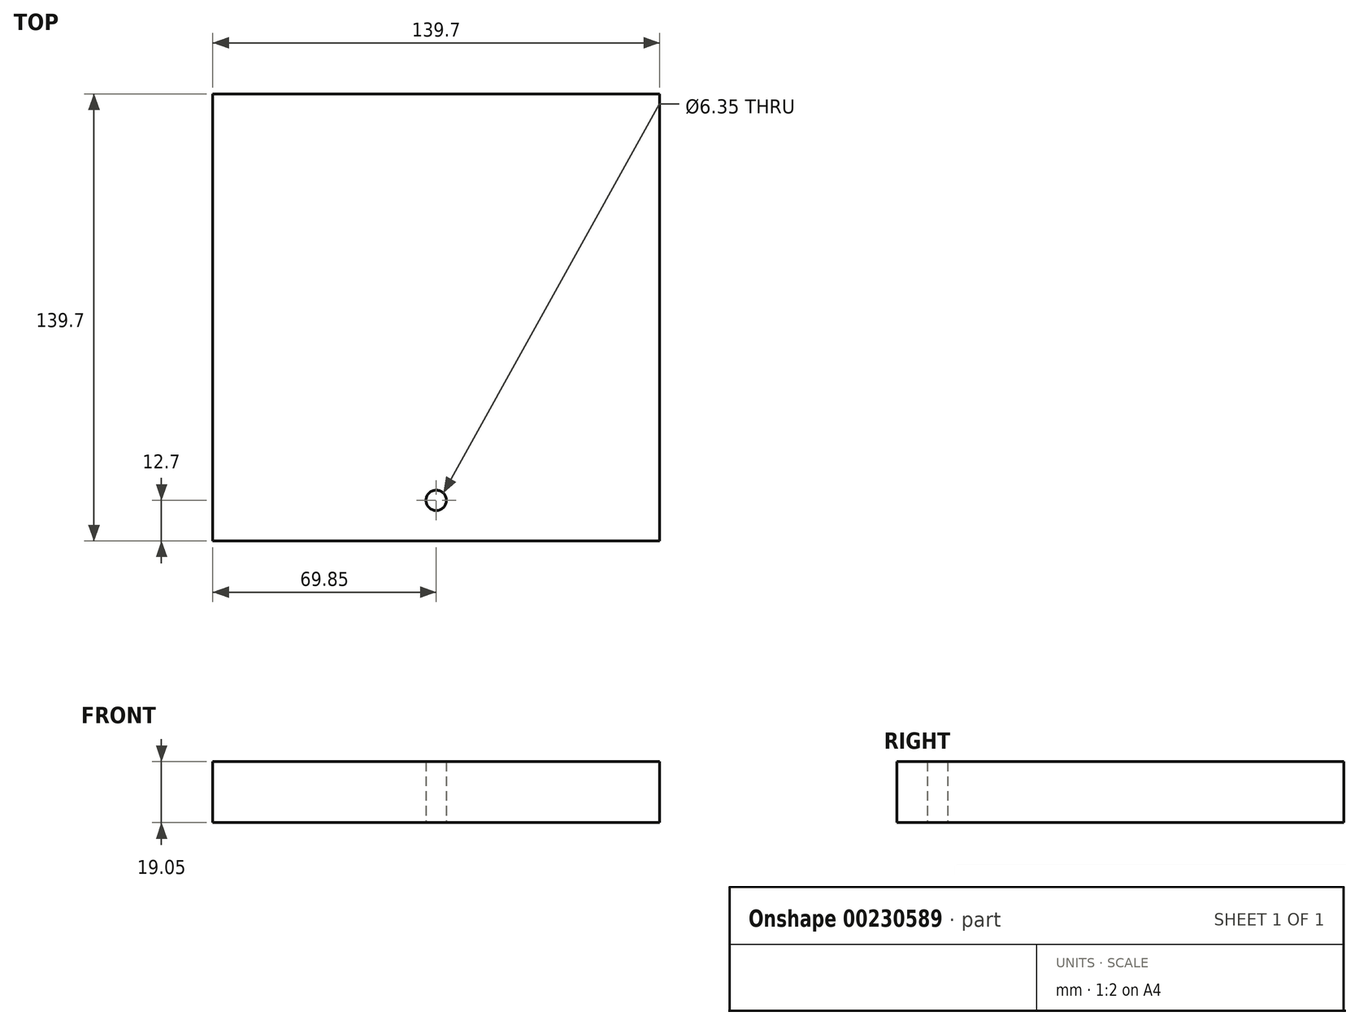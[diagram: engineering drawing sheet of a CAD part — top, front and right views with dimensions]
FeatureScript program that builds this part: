
annotation { "Feature Type Name" : "Feature", "Feature Type Description" : "" }
export const myFeature = defineFeature(function(context is Context, id is Id, definition is map)
    precondition{}
    {
        {
            var Q0;
            Q0=qCreatedBy(makeId("Top.planeOp"),FACE);
            var sketch = newSketch(context, id + "F0", { "sketchPlane" : qUnion([Q0])});
            skLineSegment(sketch, "E0.bottom", {"start": v(-69.85, 69.85) * mm, "end": v(69.85, 69.85) * mm});
            skLineSegment(sketch, "E0.top", {"start": v(-69.85, -69.85) * mm, "end": v(69.85, -69.85) * mm});
            skLineSegment(sketch, "E0.left", {"start": v(-69.85, 69.85) * mm, "end": v(-69.85, -69.85) * mm});
            skLineSegment(sketch, "E0.right", {"start": v(69.85, 69.85) * mm, "end": v(69.85, -69.85) * mm});
            skPoint(sketch, "E0.middle", {"position": v(0, 0) * mm});
            skPoint(sketch, "E1.endSnap0", {"position": v(0, -69.85) * mm});
            skCircle(sketch, "E2", {"center": v(0, -57.15) * mm, "radius": 3.18 * mm});
            skSolve(sketch);
        }
        {
            var Q0;
            Q0=makeQuery(id+"F0.imprint","IMPRINT",FACE,{"disambiguationData":[TD([[makeQuery(id+"F0.imprint","IMPRINT",EDGE,{"derivedFrom":sQuery(id+"F0.wireOp",EDGE,"E0.bottom")}),-1.0]])]});
            extrude(context, id + "F1", {"entities" : qUnion([Q0]), "depth" : 19.05 * mm});
        }
    });
